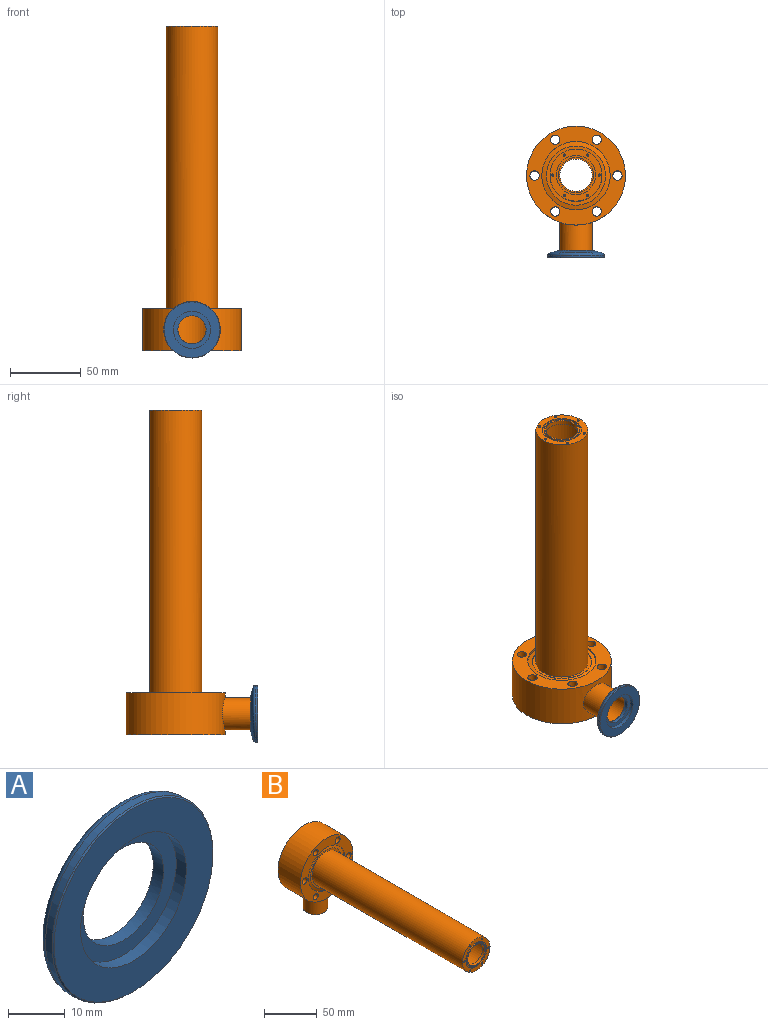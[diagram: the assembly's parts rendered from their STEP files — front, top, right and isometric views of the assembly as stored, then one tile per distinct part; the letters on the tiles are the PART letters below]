
ASSEMBLY  parts=2 mates=1
PART A: 9 faces, bbox 43.3x5.1x43.3 mm
  f0: cylinder r=10mm len=20mm, axis (0,1,0), area 162.1mm2, adj f6,f8
  f1: cone r=20mm half-angle=45deg, axis (0,1,0), area 44.2mm2, adj f4,f7
  f2: torus R=18.5mm, axis (0,-1,0), area 241.9mm2, adj f3,f4
  f3: cone r=12.24mm half-angle=75deg, axis (0,-1,0), area 673.3mm2, adj f2,f8
  f4: cylinder r=20mm len=40mm, axis (0,1,0), area 200.9mm2, adj f1,f2
  f5: cylinder r=13.15mm len=26.3mm, axis (0,1,0), area 206.6mm2, adj f6,f7
  f6: plane 26.3x26.3mm, normal (0,-1,0), area 229.1mm2, adj f0,f5
  f7: plane 39.5x39.5mm, normal (0,-1,0), area 682.2mm2, adj f1,f5
  f8: plane 24.47x24.47mm, normal (0,1,0), area 156.3mm2, adj f0,f3
PART B: 43 faces, bbox 70x230x88 mm
  f0: cone r=0mm half-angle=59deg, axis (0,-1,0), area 2.3mm2, adj f1
  f1: cylinder r=0.8mm len=2mm, axis (0,-1,0), area 10.1mm2, adj f0,f33
  f2: cone r=0mm half-angle=59deg, axis (0,-1,0), area 2.3mm2, adj f3
  f3: cylinder r=0.8mm len=2mm, axis (0,-1,0), area 10.1mm2, adj f2,f33
  f4: cone r=0mm half-angle=59deg, axis (0,-1,0), area 2.3mm2, adj f5
  f5: cylinder r=0.8mm len=2mm, axis (0,-1,0), area 10.1mm2, adj f4,f33
  f6: cone r=0mm half-angle=59deg, axis (0,-1,0), area 2.3mm2, adj f7
  f7: cylinder r=0.8mm len=2mm, axis (0,-1,0), area 10.1mm2, adj f6,f33
  f8: cone r=0mm half-angle=59deg, axis (0,-1,0), area 2.3mm2, adj f9
  f9: cylinder r=0.8mm len=2mm, axis (0,-1,0), area 10.1mm2, adj f8,f33
  f10: cylinder r=35mm len=70mm, axis (0,1,0), area 6176.1mm2, adj f17,f18,f23
  f11: cylinder r=16.9mm len=225.8mm, axis (0,1,0), area 23647.1mm2, adj f20,f25,f41
  f12: cylinder r=3.3mm len=30mm, axis (0,1,0), area 617.2mm2, adj f17,f18,f22
  f13: cylinder r=3.3mm len=30mm, axis (0,1,0), area 617.2mm2, adj f17,f18,f21
  f14: cylinder r=3.3mm len=30mm, axis (0,1,0), area 622mm2, adj f17,f18
  f15: cylinder r=3.3mm len=30mm, axis (0,1,0), area 622mm2, adj f17,f18
  f16: cylinder r=3.3mm len=30mm, axis (0,1,0), area 622mm2, adj f17,f18
  f17: plane 70x70mm, normal (0,-1,0), area 1807.1mm2, adj f10,f12,f13,f14,f15,f16,f19,f30
  f18: plane 70x70mm, normal (0,1,0), area 1807.1mm2, adj f10,f12,f13,f14,f15,f16,f19,f26
  f19: cylinder r=3.3mm len=30mm, axis (0,1,0), area 622mm2, adj f17,f18
  f20: cylinder r=10mm len=39.38mm, axis (0,0,-1), area 2368.6mm2, adj f11,f24
  f21: cylinder r=11.5mm len=3.38mm, axis (0,0,1), area 4.8mm2, adj f13
  f22: cylinder r=11.5mm len=3.38mm, axis (0,0,1), area 4.8mm2, adj f12
  f23: cylinder r=11.5mm len=23mm, axis (0,0,1), area 1370.3mm2, adj f10,f24
  f24: plane 23x23mm, normal (0,0,-1), area 101.3mm2, adj f20,f23
  f25: plane 41.9x41.9mm, normal (0,1,0), area 481.6mm2, adj f11,f28
  f26: cylinder r=24.17mm len=48.35mm, axis (0,1,0), area 226mm2, adj f18,f27
  f27: cone r=24.17mm half-angle=74.6deg, axis (0,-1,0), area 474.2mm2, adj f26,f28
  f28: cylinder r=20.95mm len=41.9mm, axis (0,1,0), area 79mm2, adj f25,f27
  f29: plane 41.9x41.9mm, normal (0,-1,0), area 315.2mm2, adj f31,f34
  f30: cylinder r=24.17mm len=48.35mm, axis (0,-1,0), area 226mm2, adj f17,f32
  f31: cylinder r=20.95mm len=41.9mm, axis (0,-1,0), area 79mm2, adj f29,f32
  f32: cone r=24.17mm half-angle=74.6deg, axis (0,1,0), area 474.2mm2, adj f30,f31
  f33: plane 36.8x36.8mm, normal (0,-1,0), area 444.6mm2, adj f1,f3,f5,f7,f9,f34,f36,f38
  f34: cylinder r=18.4mm len=201.2mm, axis (0,1,0), area 23260.9mm2, adj f29,f33
  f35: cone r=0mm half-angle=59deg, axis (0,-1,0), area 2.3mm2, adj f36
  f36: cylinder r=0.8mm len=2mm, axis (0,-1,0), area 10.1mm2, adj f33,f35
  f37: cylinder r=12.4mm len=24.8mm, axis (0,-1,0), area 87.7mm2, adj f39,f40
  f38: cylinder r=13.9mm len=27.8mm, axis (0,-1,0), area 98.3mm2, adj f33,f39
  f39: plane 27.8x27.8mm, normal (0,-1,0), area 123.9mm2, adj f37,f38
  f40: plane 24.8x24.8mm, normal (0,-1,0), area 74.8mm2, adj f37,f42
  f41: plane 33.8x33.8mm, normal (0,1,0), area 489mm2, adj f11,f42
  f42: cylinder r=11.4mm len=22.8mm, axis (0,-1,0), area 214.9mm2, adj f40,f41
PLACE A t=(1.03,-59.51,-86.35)mm
PLACE B rot(axis=(-1,0,0),90deg) t=(1.03,-1.43,-101.35)mm
MATE planar B.f20 <-> A.f0  axis (0,-1,0) through (1.03,-54.43,-86.35)mm
